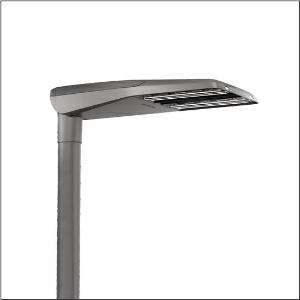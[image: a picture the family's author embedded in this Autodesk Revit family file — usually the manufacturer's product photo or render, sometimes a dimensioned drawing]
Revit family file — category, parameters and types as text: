
# Revit family: streetlight_sl_11_iq_midi___st1_0ab_5xc3n51f08me_d360
name_source: partatom
category: Lighting Fixtures
units: mm (PartAtom-declared; Revit-internal decimal feet)

## family parameters
Cut with Voids When Loaded = No
Host = Face
Light Source = No
Part Type = Normal
Room Calculation Point = No
Round Connector Dimension = Use Diameter
Shared = No

## types (1)
- --- (1 x LED, 15260 lm, 124.7 W, 3000K)
    Apparent Load = 125 VA
    CIE Flux Codes = 29 63 95 100 100
    Color Rendering = 70
    Color Temperature = 3000K
    Default Elevation = 1800 mm
    Description = Streetlight SL 11 iQ midi, mast luminaire, primary light control with 3 zone facetted reflector, of plastic, silver coated, highly specular, primary optical cover: cover, of PMMA, transparent, light distribution: ST1.0aB, light emission: direct distribution, primary light characteristic: asymmetric, installation type: post-top, side-entry, LED, High Power LED, rated luminous flux: 15.260lm, luminous efficacy: 122lm/W, light colour: 730, colour temperature: 3000K, control: optimised constant luminous flux control (CLO 2.0), Street-Remote, Desk-Remote (wireless, voltage-free reading and setting of iQ features in the workshop via application-optimized NFC function/RFID function), Light-Fading, Smart-Wire, Night-Set, Lumen-Switch, Temp-Guard, Auto-Match, with cable H07RN-F 5x 1.5mm², mains connection: 230..240V, AC, 50/60Hz, connection cable pre-assembled, cable length: 12,5m, start of lifetime: 125W, end of service life: 132W, reduction: 57W, luminaire housing, of diecast aluminium, powder-coated, Siteco® metallic grey (DB 702S), please order mast flange separately, inclination adjustable without tools: 0°, 5°, 10°, 15° (post-top) | 0°, -5°, -10°, -15° (side-entry), sealing non-destructively replaceable, multi-level sealing system, length: 780mm, width: 376mm, height: 118mm, mast flange for spigot size: 42mm (side-entry): 5XC10008XM4, 60/48mm (side-entry/post-top): 5XC10108XM2, 76/60mm (side-entry/post-top): 5XC10108XM1, equipment: Power, protection rating (complete): IP66, insulation class (complete): insulation class II (safety insulation), certification: CE, ENEC, VDE, impact resistance: IK09, permissible operating ambient temperature for outdoor applications: -25..+50°C, standard-compliant lighting for roads and squares, Environmental Product Declaration (EPD) tested and certified by an independent institute, packaging unit: 1 piece

Light Distribution: ST1.0aB
    Height = 118 mm
    Lamp = 1 x LED
    Lamp Light Flux = 15260 lm
    Lamp Power = 124.7 W
    Lamp count = 1
    Length = 780 mm
    Luminous efficacy = 122 lm/W
    Manufacturer = Siteco
    ModVariant = No
    Model = 5XC3N51F08ME
    Number of Poles = 1
    OnlyDefault = Yes
    Power Factor = 1
    Product Name = Streetlight SL 11 iQ midi | ST1.0aB
    Product group = mast luminaire | pylon top
    ProductGroupID = 6100
    Protection Class = Protection class II
    Protection Degree = IP 66
    RLX_Detail_Level = 1
    RLX_Emergency_Light_Flux = 0 lm
    RLX_Emergency_Type = 0
    RLX_Emergency_Type_DB = No
    RlxData = <blob elided: 70037 chars, md5=3a5660ba>
    Socket = socket
    Standby Power = 0 W
    System Light Flux = 15260 lm
    System Power = 125 W
    Type Comments = factory setting: luminous flux: 100 % | dim-lin: 254 | 557 mA
    Type Image = l_1005960.jpg
    URL = http://relux.com
    VarID = @adj_020145
    Voltage = 0 V
    Weight = 0.00 kg
    Width = 376 mm

## geometry (parser evidence)
native form markers: Blend x4, Sweep x10
no freeform markers — native parametric forms only
